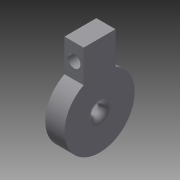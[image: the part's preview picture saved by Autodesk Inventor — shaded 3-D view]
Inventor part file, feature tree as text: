
AUTODESK INVENTOR PART (.ipt)
format: ipt  version: 2015 SP1 (Build 190203100, 203)  size: 117,760 bytes
history: native  units: mm
features: extrude x5, sketch x5, other x1, fillet x1, projected_geometry x1
ambient origin geometry x8: Origin, YZ Plane, XZ Plane, XY Plane, X Axis, Y Axis, Z Axis, Center Point
bodies: Body1 (feature_tree)
feature tree (13):
  other  "Sólido1"
  extrude  "Extrusión1"  Depth=11.0mm
  extrude  "Extrusión2"  Depth=10.0mm
  extrude  "Extrusión3"  Depth=5.0mm
  extrude  "Extrusión4"  Depth=5.0mm TaperAngle=0.0deg
  extrude  "Extrusión5"  Depth=2.0mm
  fillet  "Empalme1"  Radius=1.0mm
  sketch  "Boceto1"  dims[d0=4.2mm d1=11.0mm]
  sketch  "Boceto2"  dims[d2=3.0mm d3=0.0mm d4=10.0mm]
  sketch  "Boceto3"  dims[d5=2.5mm d6=5.0mm]
  projected_geometry  "Contorno proyectado1"
  sketch  "Boceto4"  dims[d7=3.0mm d8=0.0mm d11=5.0mm d12=0.0mm]
  sketch  "Boceto5"  dims[d13=1.0mm d14=0.0mm d15=1.5mm d16=1.0mm d17=0.0mm d18=1.0mm d19=2.0mm]
